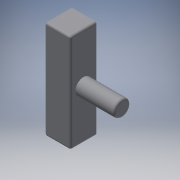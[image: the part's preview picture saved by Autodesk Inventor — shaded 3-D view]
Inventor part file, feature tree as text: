
AUTODESK INVENTOR PART (.ipt)
format: ipt  version: 2018 (Build 220112000, 112)  size: 189,952 bytes
history: native  units: in
note: dims shown in document units (in); Inventor stores cm internally (conversion verified against a paired STEP export)
features: extrude x4, sketch x4, fillet x3, other x3, reference x2
ambient origin geometry x8: Origin, YZ Plane, XZ Plane, XY Plane, X Axis, Y Axis, Z Axis, Center Point
bodies: Solid1 (feature_tree)
feature tree (16):
  extrude  "Extrusion1"  Depth=0.5in
  extrude  "Extrusion2"  Depth=0.25in
  extrude  "Extrusion3"  Depth=0.25in
  fillet  "Fillet1"  Radius=0.1181in
  fillet  "Fillet2"  Radius=0.949in
  fillet  "Fillet3"  Radius=0.1181in
  extrude  "Extrusion5"  Depth=0.3543in
  sketch  "Sketch1"  dims[d0=0.75in d1=0.5in]
  reference  "Reference1"
  reference  "Reference2"
  sketch  "Sketch2"  dims[d2=0.125in d3=0.25in]
  sketch  "Sketch3"  dims[d4=0.1181in d5=0.25in d6=0.1181in d7=0.949in d8=0.1181in]
  sketch  "Sketch5"  dims[d9=0.5in d10=0.0in d11=1.199in d12=0.25in d13=0.311in d14=0.75in d15=0.0in d16=0.75in d17=0.5in d18=0.125in d19=0.25in d20=0.1181in d21=0.25in d22=0.1181in d23=0.949in d24=0.1181in d25=100.0in d26=0.0in d27=2.3985in d28=0.25in d29=0.25in d45=0.0394in d46=0.0394in d47=0.0394in d48=0.0787in d49=0.1181in d50=0.0984in d51=0.3543in d52=0.0in]
  other  "<userpath>\OneDrive\Documents\Inventor\TSA\2018\Animatronics\Tortoise\AssemblyTURTLE.iam"
  other  "AssemblyTURTLE.iam"
  other  "Frame:1"
